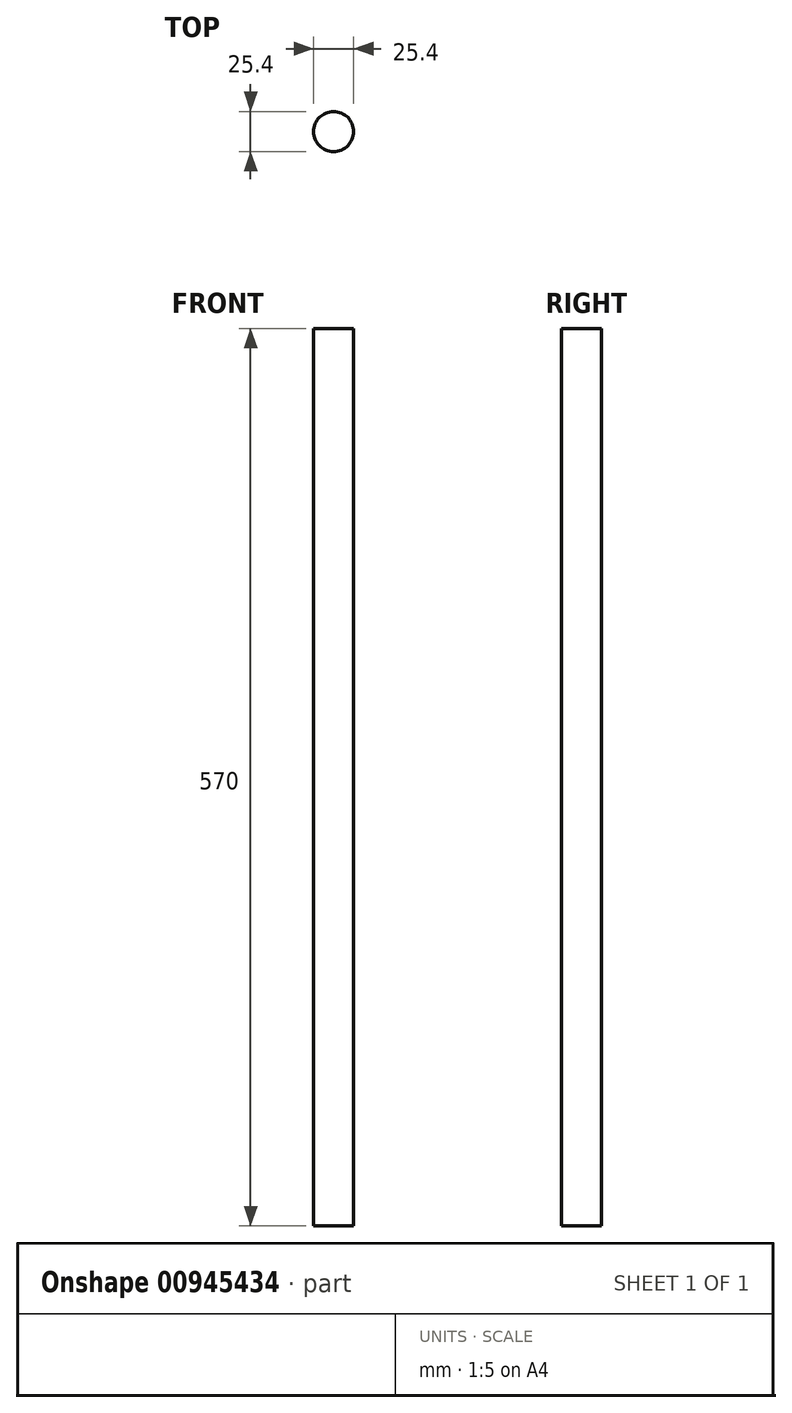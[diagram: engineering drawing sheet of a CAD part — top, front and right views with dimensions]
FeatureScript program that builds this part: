
annotation { "Feature Type Name" : "Feature", "Feature Type Description" : "" }
export const myFeature = defineFeature(function(context is Context, id is Id, definition is map)
    precondition{}
    {
        {
            var Q0;
            Q0=qCreatedBy(makeId("Top.planeOp"),FACE);
            var sketch = newSketch(context, id + "F0", { "sketchPlane" : qUnion([Q0])});
            skCircle(sketch, "E0", {"center": v(0, 0) * mm, "radius": 12.7 * mm});
            skSolve(sketch);
        }
        {
            var Q0;
            Q0=sQuery(id+"F0.wireOp",EDGE,"E0");
            extrude(context, id + "F1", {"bodyType" : ToolBodyType.SURFACE, "surfaceEntities" : qUnion([Q0]), "depth" : 570 * mm, "offsetDistance" : 25.4 * mm});
        }
    });
